# Revit family: EURS_63_LF_FB_BY481P
name_source: partatom
category: Lighting Fixtures
units: mm (PartAtom-declared; Revit-internal decimal feet)

## family parameters
Cut with Voids When Loaded = No
Host = Face
Light Source = No
Part Type = Normal
Room Calculation Point = No
Round Connector Dimension = Use Diameter
Shared = No

## types (1)
- EURS_63_LF_FB_BY481P
    12NC = 12NC CODE
    Apparent Load = 0 VA
    BIM Library - URL = http://www.lighting.philips.com
    Ceiling thickness = 13 mm  [stored 0.0426509 ft]
    Content modified date = DATE
    Content version = 1.0
    Default Elevation = 0 mm  [stored 0 ft]
    Description = MODEL NAME
    EOC = EOC CODE
    ETIM code = MODEL ETIM CODE
    ETIM code URL = ETIM CODE WEBPAGE
    Fixture code = FIXTURE CODE
    Height = 50 mm  [stored 0.164042 ft]
    Lamp = LAMP NAME
    Lamp type = BY481P IES Data : PSD 1 xLED250S_840 HRO
    Last IES update = DATE
    Length = 600 mm  [stored 1.9685 ft]
    Light source = 2 mm  [stored 0.00656168 ft]
    Manufacturer = Philips
    Model = MODEL NUMBER
    Order code = ORDER CODE
    Product catalog - URL = MODEL WEBPAGE
    Type Comments = Pendant
    URL = http://www.lighting.philips.com
    Voltage (V) = 230 V
    Width = 490 mm  [stored 1.60761 ft]

note: [stored X ft] marks values corroborated as IEEE doubles in the binary element streams (Revit-internal decimal feet)

## geometry (parser evidence)
native form markers: Blend x2, Sweep x10
no freeform markers — native parametric forms only
